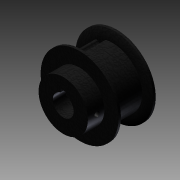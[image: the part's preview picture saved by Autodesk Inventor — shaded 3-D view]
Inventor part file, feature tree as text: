
AUTODESK INVENTOR PART (.ipt)
format: ipt  version: 2012 (Build 160160000, 160)  size: 195,584 bytes
history: native  units: in
note: dims shown in document units (in); Inventor stores cm internally (conversion verified against a paired STEP export)
features: extrude x1, imported_body x1, sketch x1
ambient origin geometry x8: Origin, YZ Plane, XZ Plane, XY Plane, X Axis, Y Axis, Z Axis, Center Point
feature tree (3):
  extrude  "Extrusion1"  Depth=0.0787in
  imported_body  "Base1"
  sketch  "Sketch2"  dims[d1=0.0787in d2=0.0787in d3=0.0394in d4=0.3157in d5=0.1972in d6=0.3937in d7=0.0in]
